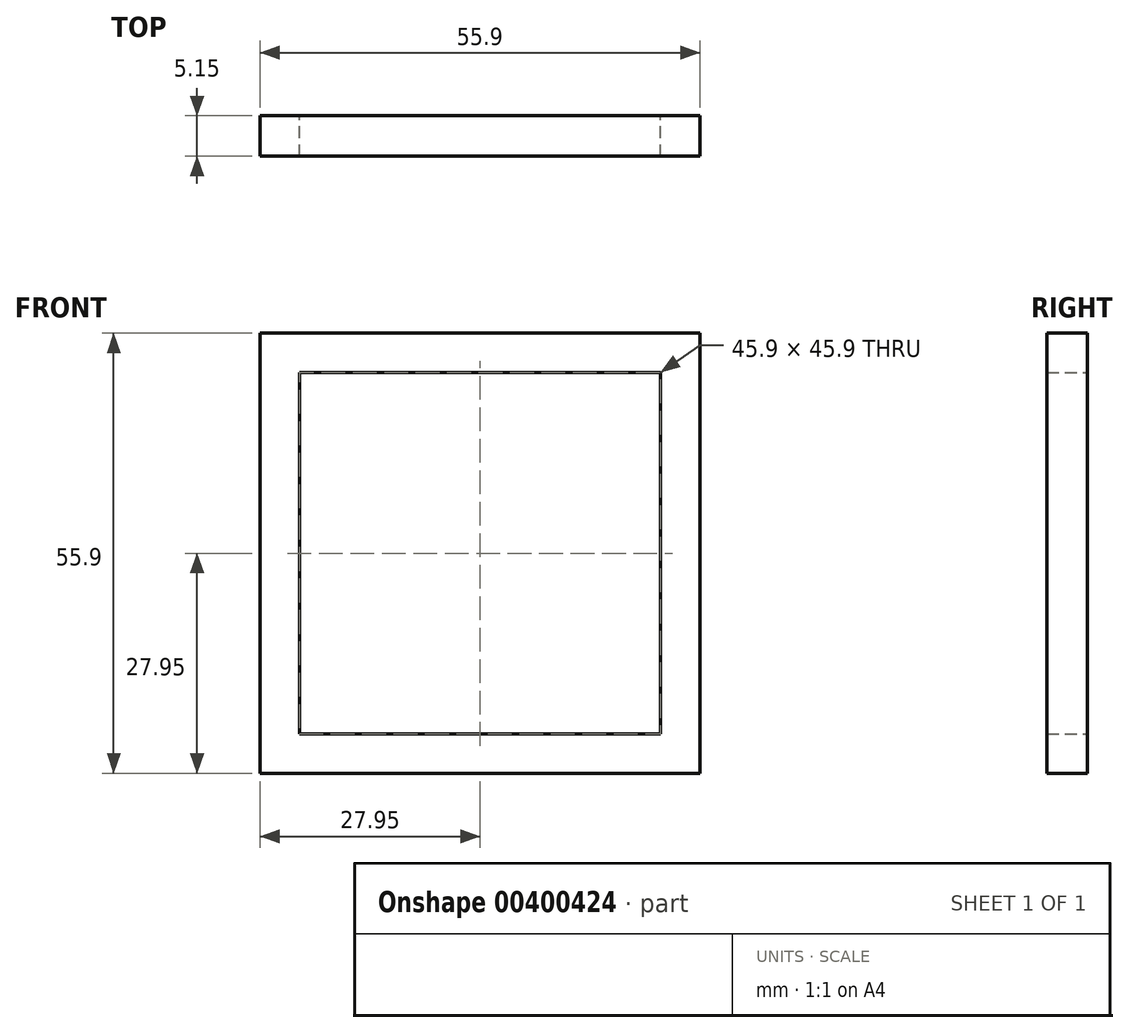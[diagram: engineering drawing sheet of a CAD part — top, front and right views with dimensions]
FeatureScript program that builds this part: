
annotation { "Feature Type Name" : "Feature", "Feature Type Description" : "" }
export const myFeature = defineFeature(function(context is Context, id is Id, definition is map)
    precondition{}
    {
        {
            var Q0;
            Q0=qCreatedBy(makeId("Front.planeOp"),FACE);
            var sketch = newSketch(context, id + "F0", { "sketchPlane" : qUnion([Q0])});
            skLineSegment(sketch, "E0.bottom", {"start": v(0, 0) * mm, "end": v(55.9, 0) * mm});
            skLineSegment(sketch, "E0.top", {"start": v(0, -55.9) * mm, "end": v(55.9, -55.9) * mm});
            skLineSegment(sketch, "E0.left", {"start": v(0, 0) * mm, "end": v(0, -55.9) * mm});
            skLineSegment(sketch, "E0.right", {"start": v(55.9, 0) * mm, "end": v(55.9, -55.9) * mm});
            skLineSegment(sketch, "E1.0", {"start": v(5, -50.9) * mm, "end": v(50.9, -50.9) * mm});
            skLineSegment(sketch, "E1.1", {"start": v(5, -5) * mm, "end": v(5, -50.9) * mm});
            skLineSegment(sketch, "E1.2", {"start": v(5, -5) * mm, "end": v(50.9, -5) * mm});
            skLineSegment(sketch, "E1.3", {"start": v(50.9, -5) * mm, "end": v(50.9, -50.9) * mm});
            skSolve(sketch);
        }
        {
            var Q0;
            Q0=makeQuery(id+"F0.imprint","IMPRINT",FACE,{"disambiguationData":[TD([[makeQuery(id+"F0.imprint","IMPRINT",EDGE,{"derivedFrom":sQuery(id+"F0.wireOp",EDGE,"E0.bottom")}),-1.0]])]});
            extrude(context, id + "F1", {"entities" : qUnion([Q0]), "depth" : 5.15 * mm});
        }
    });
